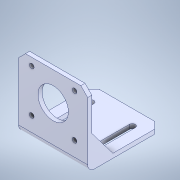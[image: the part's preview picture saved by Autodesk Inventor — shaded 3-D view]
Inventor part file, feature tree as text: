
AUTODESK INVENTOR PART (.ipt)
format: ipt  version: 2022 (Build 260153000, 153)  size: 141,824 bytes
history: mixed  units: in
note: dims shown in document units (in); Inventor stores cm internally (conversion verified against a paired STEP export)
features: fillet x1, imported_body x1
ambient origin geometry x8: Origin, YZ Plane, XZ Plane, XY Plane, X Axis, Y Axis, Z Axis, Center Point
bodies: Solid1 (imported_parasolid)
feature tree (2):
  fillet  "Fillet1"  Radius=0.0197in
  imported_body  NMx_Import_Brep_tag  [imported B-rep: ~32 faces, bbox_mm=[50.0, 52.145, 53.3]]
